# Revit family: CAME_Турникет_Полноростовой_GUARDIAN_EcoLine300ТрехсекционныйМоторизированный
name_source: partatom
category: Специальное оборудование
units: mm (PartAtom-declared; Revit-internal decimal feet)

## family parameters
Всегда вертикально = Да
На основе рабочей плоскости = Нет
Общий = Нет
При загрузке вырезать с полостями = Нет
Размер круглого соединителя = Использовать диаметр
Тип детали = Нормальный
Точка расчета площади = Нет

## types (1)
- CAME_Турникет_Полноростовой_GUARDIAN_EcoLine300ТрехсекционныйМоторизированный
    ADSK_URL документации изделия = https://camerussia.com
    ADSK_URL страницы изделия = https://camerussia.com
    ADSK_Версия Revit = 2019
    ADSK_Версия семейства = 1.0
    ADSK_Группирование = GUARDIAN
    ADSK_Единица измерения = шт.
    ADSK_Завод-изготовитель = CAME
    ADSK_Классификация нагрузок = Прочее
    ADSK_Код изделия = Код КСР 26.30.50.119.61.2.07.09
    ADSK_Количество = 1
    ADSK_Количество фаз = 1
    ADSK_Коэффициент мощности = 0.96
    ADSK_Марка = АРТ:001PSGS3E
    ADSK_Масса = 150
    ADSK_Масса_Текст = 150 кг
    ADSK_Наименование = Турникет полноростовый моторизованный GUARDIAN ECO LINE 300, трехсекционный
    ADSK_Наименование краткое = Турникет GUARDIAN ECO LINE 300 3-секц.
    ADSK_Напряжение = 230 В
    ADSK_Номинальная мощность = 20 Вт
    ADSK_Обозначение = ТУ 26.30.50-001-89603926-2021
    ADSK_Полная мощность = 21 В·А
    ADSK_Размер_Высота = 2180 мм
    ADSK_Размер_Глубина = 1240 мм
    ADSK_Размер_Ширина = 1490 мм
    BL_BIM library = https://bimlib.pro
    CAME_Диапазон рабочих температур (°C) = -20 ÷ +68
    CAME_Интенсивность использования (%) = ИНТЕНСИВНОЕ
    CAME_Класс защиты (IP) = 56
    CAME_Максимальное количество проходов в минуту = 10-25
    CAME_Напряжение электропитания двигателя (В) = 24 В
    CAME_Тип механизма турникета = моторизированный
    URL = https://camerussia.com
    Группа модели = Турникеты
    Изготовитель = CAME
    Кол = 9
    Описание = Автоматический моторизованный полноростовый турникет с корпусом, ротором и преградами из оцинкованной окрашенной стали. Три сектора по 120 градусов. Встроенный блок управления. Освещение зоны прохода. Встроенный блок питания.
    Шаг = 200 мм
